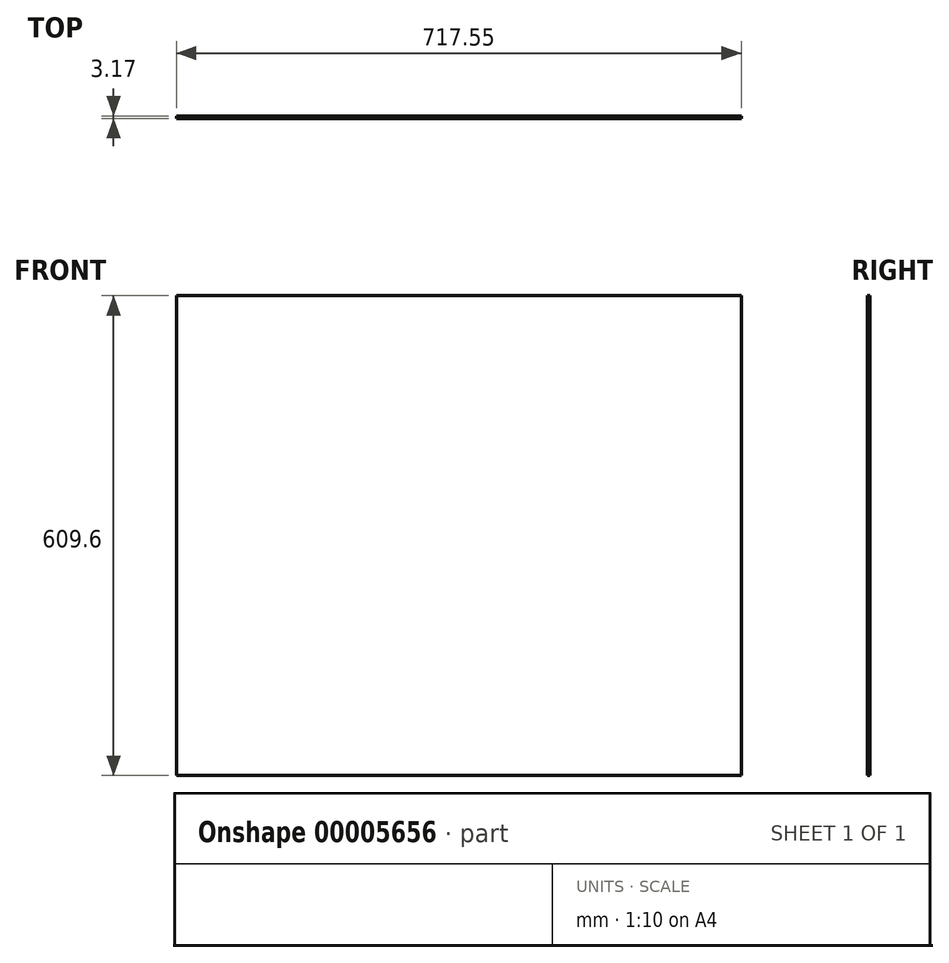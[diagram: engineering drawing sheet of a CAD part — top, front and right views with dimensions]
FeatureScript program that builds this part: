
annotation { "Feature Type Name" : "Feature", "Feature Type Description" : "" }
export const myFeature = defineFeature(function(context is Context, id is Id, definition is map)
    precondition{}
    {
        {
            var Q0;
            Q0=qCreatedBy(makeId("Front.planeOp"),FACE);
            var sketch = newSketch(context, id + "F0", { "sketchPlane" : qUnion([Q0])});
            skLineSegment(sketch, "E0.bottom", {"start": v(0, 0) * mm, "end": v(-717.55, 0) * mm});
            skLineSegment(sketch, "E0.top", {"start": v(0, 609.6) * mm, "end": v(-717.55, 609.6) * mm});
            skLineSegment(sketch, "E0.left", {"start": v(0, 0) * mm, "end": v(0, 609.6) * mm});
            skLineSegment(sketch, "E0.right", {"start": v(-717.55, 0) * mm, "end": v(-717.55, 609.6) * mm});
            skSolve(sketch);
        }
        {
            var Q0;
            Q0 = qSketchRegion(id + "F0", true);
            extrude(context, id + "F1", {"entities" : qUnion([Q0]), "depth" : 3.17 * mm});
        }
    });
